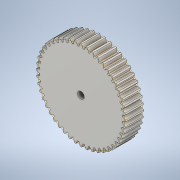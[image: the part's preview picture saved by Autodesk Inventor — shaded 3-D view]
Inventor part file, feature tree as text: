
AUTODESK INVENTOR PART (.ipt)
format: ipt  version: 2021 (Build 250183000, 183)  size: 342,528 bytes
history: native  units: mm (DEFAULTED — no unit token found)
features: plane x3, other x3, sketch x3, extrude x1, hole x1
ambient origin geometry x8: Origin, YZ Plane, XZ Plane, XY Plane, X Axis, Y Axis, Z Axis, Center Point
bodies: Solid1 (feature_tree)
feature tree (11):
  extrude  "Extrusion1"  Depth=8.0mm TaperAngle=0.0deg
  plane  "Work Plane2"
  plane  "Work Plane8"
  plane  "Work Plane9"
  other  "Spur Gear"
  hole  "Hole1"  [1 undecoded]
  sketch  "Sketch1"  dims[d0=39.68mm d1=8.0mm d2=0.0mm]
  sketch  "Sketch2"  dims[d3=38.4mm d4=10.0mm d5=0.0mm]
  other  "Srf1"
  sketch  "Sketch3"  dims[d16=28.8mm d17=0.0mm d34=0.654498mm d39=0.0mm d41=0.0mm d43=28.8mm d46=28.8mm d47=0.0mm d48=0.0mm d49=3.0mm d50=3.0mm d51=6.0mm d52=4.0mm d53=2.0mm d54=90.0deg d55=8.0mm d56=20.594885mm]
  other  "Pitch Diameter"
note: 1 required parameter value undecoded (feature->parameter linkage not recoverable at this tier; creation-order binding heuristic only, values carry confidence <= 0.55)
